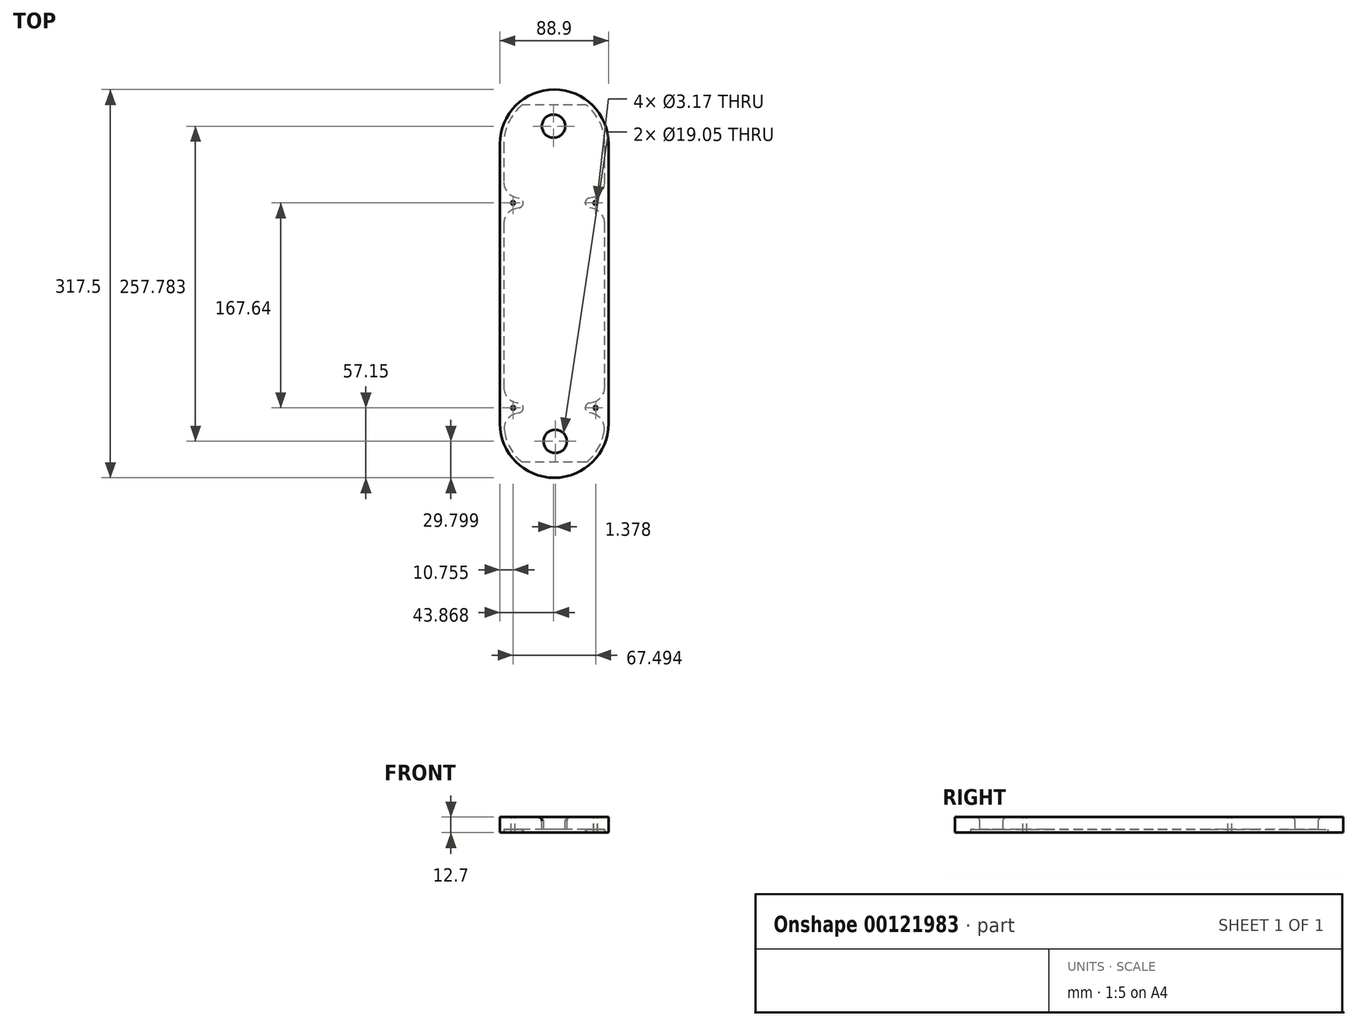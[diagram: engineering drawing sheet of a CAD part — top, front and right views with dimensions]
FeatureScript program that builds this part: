
annotation { "Feature Type Name" : "Feature", "Feature Type Description" : "" }
export const myFeature = defineFeature(function(context is Context, id is Id, definition is map)
    precondition{}
    {
        {
            var Q0;
            Q0=qCreatedBy(makeId("Top.planeOp"),FACE);
            var sketch = newSketch(context, id + "F0", { "sketchPlane" : qUnion([Q0])});
            skLineSegment(sketch, "E0.bottom", {"start": v(0, 317.5) * mm, "end": v(88.9, 317.5) * mm, "construction": true});
            skLineSegment(sketch, "E0.top", {"start": v(0, 0) * mm, "end": v(88.9, 0) * mm, "construction": true});
            skLineSegment(sketch, "E0.left", {"start": v(0, 317.5) * mm, "end": v(0, 0) * mm, "construction": true});
            skLineSegment(sketch, "E0.right", {"start": v(88.9, 317.5) * mm, "end": v(88.9, 0) * mm, "construction": true});
            skLineSegment(sketch, "E1", {"start": v(-24.65, 57.15) * mm, "end": v(106.19, 57.15) * mm, "construction": true});
            skLineSegment(sketch, "E2", {"start": v(-23.74, 224.8) * mm, "end": v(107.73, 224.8) * mm, "construction": true});
            skLineSegment(sketch, "E3", {"start": v(19.05, 335.91) * mm, "end": v(19.05, -37.54) * mm, "construction": true});
            skLineSegment(sketch, "E4", {"start": v(69.85, -32.17) * mm, "end": v(69.85, 331.93) * mm, "construction": true});
            skCircle(sketch, "E5", {"center": v(14.92, 224.8) * mm, "radius": 4.13 * mm, "construction": true});
            skCircle(sketch, "E6", {"center": v(73.98, 224.8) * mm, "radius": 4.13 * mm, "construction": true});
            skCircle(sketch, "E7", {"center": v(14.92, 57.15) * mm, "radius": 4.13 * mm, "construction": true});
            skCircle(sketch, "E8", {"center": v(73.98, 57.15) * mm, "radius": 4.13 * mm, "construction": true});
            skCircle(sketch, "E9", {"center": v(45.25, 29.8) * mm, "radius": 9.53 * mm, "construction": true});
            skLineSegment(sketch, "E10.bottom", {"start": v(60.32, 228.6) * mm, "end": v(63.5, 228.6) * mm, "construction": true});
            skLineSegment(sketch, "E10.top", {"start": v(60.32, 38.1) * mm, "end": v(63.5, 38.1) * mm, "construction": true});
            skLineSegment(sketch, "E10.left", {"start": v(60.32, 228.6) * mm, "end": v(60.32, 38.1) * mm, "construction": true});
            skLineSegment(sketch, "E10.right", {"start": v(63.5, 228.6) * mm, "end": v(63.5, 38.1) * mm, "construction": true});
            skCircle(sketch, "E11", {"center": v(43.87, 287.58) * mm, "radius": 9.53 * mm, "construction": true});
            skLineSegment(sketch, "E12.bottom", {"start": v(25.4, 298.45) * mm, "end": v(28.57, 298.45) * mm, "construction": true});
            skLineSegment(sketch, "E12.top", {"start": v(25.4, 69.85) * mm, "end": v(28.57, 69.85) * mm, "construction": true});
            skLineSegment(sketch, "E12.left", {"start": v(25.4, 298.45) * mm, "end": v(25.4, 69.85) * mm, "construction": true});
            skLineSegment(sketch, "E12.right", {"start": v(28.57, 298.45) * mm, "end": v(28.57, 69.85) * mm, "construction": true});
            skLineSegment(sketch, "E13", {"start": v(52.81, 133.35) * mm, "end": v(108.8, 133.35) * mm, "construction": true});
            skSolve(sketch);
        }
        {
            var Q0;
            Q0=qCreatedBy(makeId("Top.planeOp"),FACE);
            var sketch = newSketch(context, id + "F1", { "sketchPlane" : qUnion([Q0])});
            skLineSegment(sketch, "E14", {"start": v(0, 273.05) * mm, "end": v(0, 44.45) * mm});
            skLineSegment(sketch, "E15", {"start": v(88.9, 44.45) * mm, "end": v(88.9, 273.05) * mm});
            skArc(sketch, "E16", {"start": v(88.9, 273.05) * mm, "mid": v(44.45, 317.5) * mm, "end": v(0, 273.05) * mm});
            skArc(sketch, "E17", {"start": v(0, 44.45) * mm, "mid": v(44.45, 0) * mm, "end": v(88.9, 44.45) * mm});
            skCircle(sketch, "E18", {"center": v(10.85, 57.15) * mm, "radius": 1.59 * mm});
            skCircle(sketch, "E19", {"center": v(78.25, 57.15) * mm, "radius": 1.59 * mm});
            skCircle(sketch, "E20", {"center": v(78.07, 224.8) * mm, "radius": 1.59 * mm});
            skCircle(sketch, "E21", {"center": v(10.75, 224.8) * mm, "radius": 1.59 * mm});
            skCircle(sketch, "E22", {"center": v(45.25, 29.8) * mm, "radius": 9.53 * mm});
            skCircle(sketch, "E23", {"center": v(43.87, 287.58) * mm, "radius": 9.53 * mm});
            skSolve(sketch);
        }
        {
            var Q0;
            Q0 = qSketchRegion(id + "F1", true);
            extrude(context, id + "F2", {"entities" : qUnion([Q0]), "oppositeDirection" : true, "depth" : 12.7 * mm});
        }
        {
            var Q0;
            Q0=makeQuery(id+"F2.opExtrude","CAP_FACE",FACE,{"disambiguationData":[OSD([sQuery(id+"F1.wireOp",EDGE,"E14"),sQuery(id+"F1.wireOp",EDGE,"E15"),sQuery(id+"F1.wireOp",EDGE,"E16"),sQuery(id+"F1.wireOp",EDGE,"E17"),sQuery(id+"F1.wireOp",EDGE,"5W22Nxdr-MH6h-GY9u-zvtY-ck4WT3yjX1Pc"),sQuery(id+"F1.wireOp",EDGE,"jGU5K2Bb-3kkE-ncNQ-fKEE-gM3cZbARYaye"),sQuery(id+"F1.wireOp",EDGE,"E18"),sQuery(id+"F1.wireOp",EDGE,"E19"),sQuery(id+"F1.wireOp",EDGE,"E20"),sQuery(id+"F1.wireOp",EDGE,"E21")])],"isStart":false});
            var sketch = newSketch(context, id + "F3", { "sketchPlane" : qUnion([Q0])});
            skArc(sketch, "E24.0", {"start": v(85.72, -273.05) * mm, "mid": v(81.81, -290.59) * mm, "end": v(70.82, -304.8) * mm});
            skLineSegment(sketch, "E24.1", {"start": v(85.72, -74.1) * mm, "end": v(85.72, -207.84) * mm});
            skArc(sketch, "E24.2", {"start": v(3.65, -38.22) * mm, "mid": v(8.52, -24.14) * mm, "end": v(18.08, -12.7) * mm});
            skLineSegment(sketch, "E24.3", {"start": v(3.17, -273.05) * mm, "end": v(3.17, -241.8) * mm});
            skLineSegment(sketch, "E25", {"start": v(70.82, -304.8) * mm, "end": v(18.08, -304.8) * mm});
            skLineSegment(sketch, "E26", {"start": v(70.82, -12.7) * mm, "end": v(18.08, -12.7) * mm});
            skArc(sketch, "E27", {"start": v(15.8, -228.82) * mm, "mid": v(19.05, -224.8) * mm, "end": v(15.8, -220.76) * mm});
            skArc(sketch, "E28", {"start": v(73.2, -220.74) * mm, "mid": v(69.85, -224.77) * mm, "end": v(73.17, -228.84) * mm});
            skArc(sketch, "E29", {"start": v(15.16, -61.27) * mm, "mid": v(19.03, -57.53) * mm, "end": v(15.9, -53.14) * mm});
            skLineSegment(sketch, "E30", {"start": v(75.41, -220.31) * mm, "end": v(73.2, -220.74) * mm});
            skLineSegment(sketch, "E31", {"start": v(75.51, -229.3) * mm, "end": v(73.17, -228.84) * mm});
            skLineSegment(sketch, "E32", {"start": v(13.17, -229.4) * mm, "end": v(15.8, -228.82) * mm});
            skLineSegment(sketch, "E33", {"start": v(15.8, -220.76) * mm, "end": v(13.16, -220.18) * mm});
            skLineSegment(sketch, "E34", {"start": v(73.2, -61.2) * mm, "end": v(75.44, -61.64) * mm});
            skLineSegment(sketch, "E35", {"start": v(75.28, -52.67) * mm, "end": v(73.14, -53.1) * mm});
            skLineSegment(sketch, "E36", {"start": v(15.9, -53.14) * mm, "end": v(13.17, -52.47) * mm});
            skLineSegment(sketch, "E37", {"start": v(15.16, -61.27) * mm, "end": v(15.16, -61.27) * mm});
            skArc(sketch, "E38.filletArc", {"start": v(85.72, -74.1) * mm, "mid": v(82.82, -66.02) * mm, "end": v(75.44, -61.64) * mm});
            skArc(sketch, "E39.filletArc", {"start": v(15.16, -61.27) * mm, "mid": v(6.64, -65.23) * mm, "end": v(3.18, -73.95) * mm});
            skArc(sketch, "E40.filletArc", {"start": v(3.65, -38.22) * mm, "mid": v(5.64, -47.2) * mm, "end": v(13.17, -52.47) * mm});
            skArc(sketch, "E41.filletArc", {"start": v(75.28, -52.67) * mm, "mid": v(83.12, -47.5) * mm, "end": v(85.27, -38.35) * mm});
            skLineSegment(sketch, "E42.trimOffspring", {"start": v(85.72, -241.76) * mm, "end": v(85.72, -273.05) * mm});
            skLineSegment(sketch, "E43.trimOffspring", {"start": v(3.17, -207.77) * mm, "end": v(3.17, -73.95) * mm});
            skPoint(sketch, "E44.visualSharp", {"position": v(3.17, -231.58) * mm});
            skArc(sketch, "E44.filletArc", {"start": v(13.17, -229.4) * mm, "mid": v(5.98, -233.84) * mm, "end": v(3.17, -241.8) * mm});
            skPoint(sketch, "E45.visualSharp", {"position": v(3.17, -218) * mm});
            skArc(sketch, "E45.filletArc", {"start": v(3.17, -207.77) * mm, "mid": v(5.98, -215.74) * mm, "end": v(13.16, -220.18) * mm});
            skPoint(sketch, "E46.visualSharp", {"position": v(85.72, -218.34) * mm});
            skArc(sketch, "E46.filletArc", {"start": v(75.41, -220.31) * mm, "mid": v(82.81, -215.93) * mm, "end": v(85.72, -207.84) * mm});
            skPoint(sketch, "E47.visualSharp", {"position": v(85.72, -231.34) * mm});
            skArc(sketch, "E47.filletArc", {"start": v(85.73, -241.76) * mm, "mid": v(82.84, -233.7) * mm, "end": v(75.51, -229.3) * mm});
            skArc(sketch, "E48.trimOffspring", {"start": v(70.82, -12.7) * mm, "mid": v(80.41, -24.2) * mm, "end": v(85.27, -38.35) * mm});
            skArc(sketch, "E49.trimOffspring", {"start": v(18.08, -304.8) * mm, "mid": v(7.09, -290.59) * mm, "end": v(3.17, -273.05) * mm});
            skArc(sketch, "E50", {"start": v(73.14, -53.1) * mm, "mid": v(69.85, -57.18) * mm, "end": v(73.2, -61.2) * mm});
            skLineSegment(sketch, "E51", {"start": v(62.95, -34.06) * mm, "end": v(62.95, -260.67) * mm, "construction": true});
            skSolve(sketch);
        }
        {
            var Q0;
            Q0=makeQuery(id+"F3.imprint","IMPRINT",FACE,{"disambiguationData":[TD([[makeQuery(id+"F3.imprint","IMPRINT",EDGE,{"derivedFrom":sQuery(id+"F3.wireOp",EDGE,"E24.0")}),1.0]])]});
            extrude(context, id + "F4", {"entities" : qUnion([Q0]), "operationType" : NewBodyOperationType.REMOVE, "oppositeDirection" : true, "depth" : 2.54 * mm});
        }
        {
            var Q0;
            Q0=makeQuery(id+"F2.opExtrude","CAP_EDGE",EDGE,{"disambiguationData":[OSD([sQuery(id+"F1.wireOp",EDGE,"E22")])],"isStart":true});
            var Q1;
            Q1=makeQuery(id+"F2.opExtrude","CAP_EDGE",EDGE,{"disambiguationData":[OSD([sQuery(id+"F1.wireOp",EDGE,"E22")])],"isStart":false});
            var Q2;
            Q2=makeQuery(id+"F2.opExtrude","CAP_EDGE",EDGE,{"disambiguationData":[OSD([sQuery(id+"F1.wireOp",EDGE,"E23")])],"isStart":true});
            var Q3;
            Q3=makeQuery(id+"F2.opExtrude","CAP_EDGE",EDGE,{"disambiguationData":[OSD([sQuery(id+"F1.wireOp",EDGE,"E23")])],"isStart":false});
            fillet(context, id + "F5", {"entities" : qUnion([Q0, Q1, Q2, Q3]), "radius" : 3.17 * mm, "tangentPropagation" : true, "allowEdgeOverflow" : false});
        }
    });
